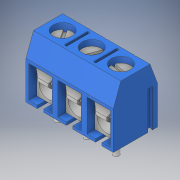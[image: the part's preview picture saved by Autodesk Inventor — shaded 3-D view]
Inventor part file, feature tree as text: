
AUTODESK INVENTOR PART (.ipt)
format: ipt  version: 2019 (Build 230136000, 136)  size: 253,440 bytes
history: native  units: in
note: dims shown in document units (in); Inventor stores cm internally (conversion verified against a paired STEP export)
features: fillet x1
ambient origin geometry x8: Origin, YZ Plane, XZ Plane, XY Plane, X Axis, Y Axis, Z Axis, Center Point
bodies: Solid1 (feature_tree)
feature tree (1):
  fillet  "Fillet2"  [1 undecoded]
note: 1 required parameter value undecoded (feature->parameter linkage not recoverable at this tier; creation-order binding heuristic only, values carry confidence <= 0.55)
